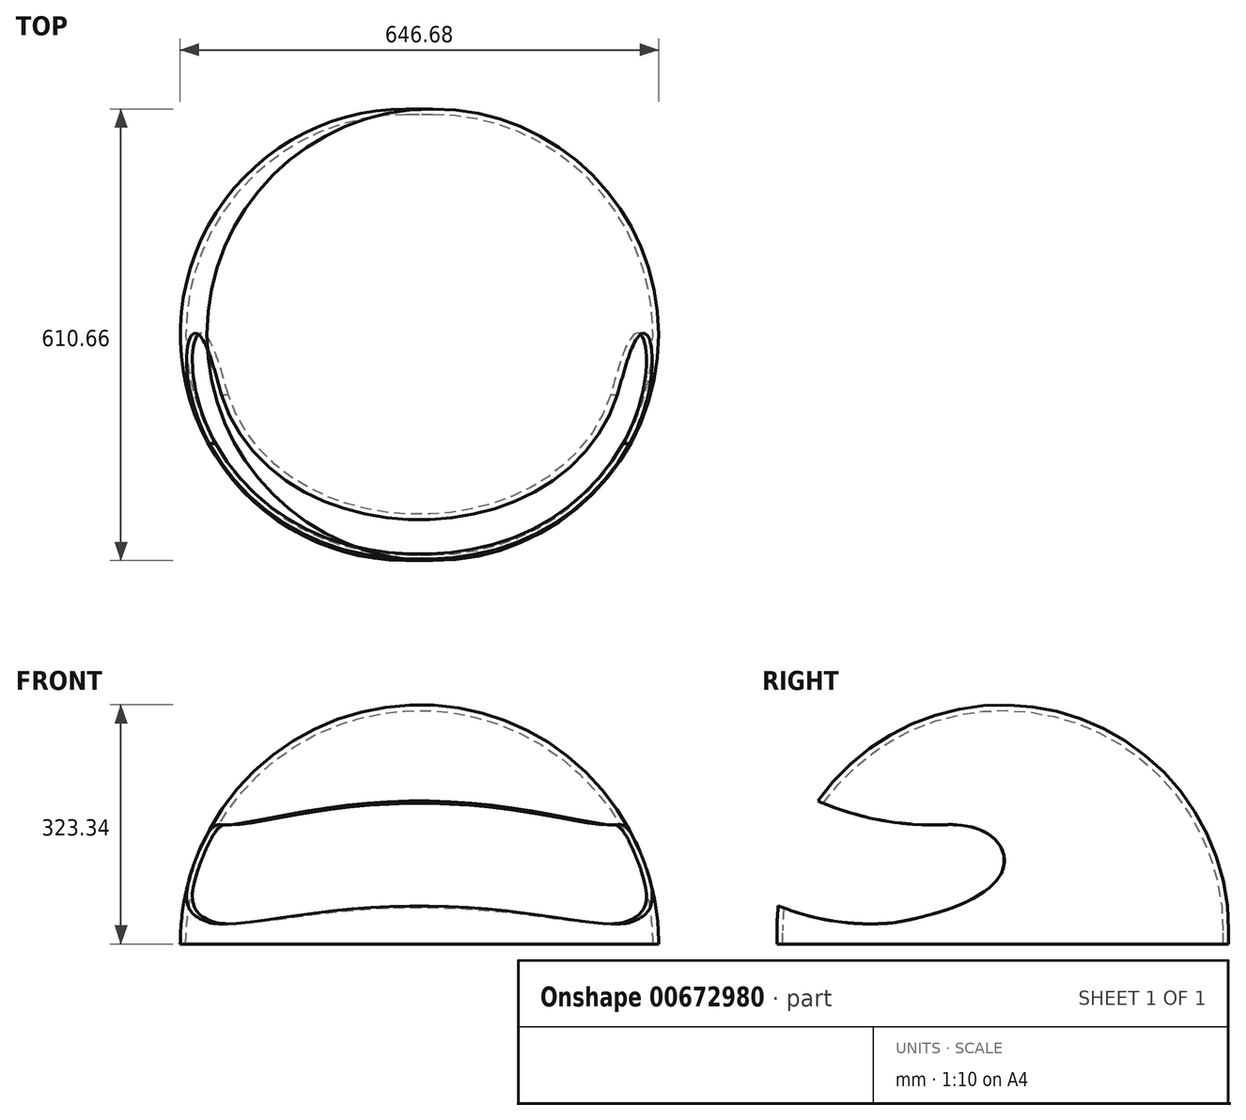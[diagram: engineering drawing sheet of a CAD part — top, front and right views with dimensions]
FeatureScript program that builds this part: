
annotation { "Feature Type Name" : "Feature", "Feature Type Description" : "" }
export const myFeature = defineFeature(function(context is Context, id is Id, definition is map)
    precondition{}
    {
        {
            var Q0;
            Q0=qCreatedBy(makeId("Top.planeOp"),FACE);
            var sketch = newSketch(context, id + "F0", { "sketchPlane" : qUnion([Q0])});
            skArc(sketch, "E0", {"start": v(0, -289.9) * mm, "mid": v(323.34, 14.9) * mm, "end": v(0, 319.7) * mm});
            skLineSegment(sketch, "E1", {"start": v(0, 341.68) * mm, "end": v(0, -321.3) * mm, "construction": true});
            skLineSegment(sketch, "E2", {"start": v(0, 319.7) * mm, "end": v(0, -289.9) * mm});
            skSolve(sketch);
        }
        {
            var Q0;
            Q0 = qSketchRegion(id + "F0", true);
            var Q1;
            Q1=sQuery(id+"F0.wireOp",EDGE,"E0");
            var Q2;
            Q2=sQuery(id+"F0.wireOp",EDGE,"E1");
            revolve(context, id + "F1", {"entities" : qUnion([Q0]), "surfaceEntities" : qUnion([Q1]), "axis" : qUnion([Q2]), "revolveType" : RevolveType.TWO_DIRECTIONS, "angle" : 180 * degree, "angleBack" : 360 * degree});
        }
        {
            var Q0;
            Q0=makeQuery(id+"F1.opRevolve","CAP_FACE",FACE,{"disambiguationData":[OSD([sQuery(id+"F0.wireOp",EDGE,"E0"),sQuery(id+"F0.wireOp",EDGE,"E2")])],"isStart":false});
            shell(context, id + "F2", {"entities" : qUnion([Q0]), "thickness" : 7.62 * mm});
        }
        {
            var Q0;
            Q0=qCreatedBy(makeId("Right.planeOp"),FACE);
            cPlane(context, id + "F3", {"entities" : qUnion([Q0]), "cplaneType" : CPlaneType.OFFSET, "offset" : 497.84 * mm, "width" : 152.4 * mm, "height" : 152.4 * mm});
        }
        {
            var Q0;
            Q0=qCreatedBy(id+"F3.planeOp",FACE);
            var sketch = newSketch(context, id + "F4", { "sketchPlane" : qUnion([Q0])});
            skArc(sketch, "E3", {"start": v(-315.15, 239.57) * mm, "mid": v(-197.38, 179.23) * mm, "end": v(-66.3, 161.05) * mm});
            skArc(sketch, "E4", {"start": v(-400.55, 126.3) * mm, "mid": v(-277.43, 47.22) * mm, "end": v(-132.27, 28.7) * mm});
            skLineSegment(sketch, "E5", {"start": v(-315.15, 239.57) * mm, "end": v(-400.55, 126.3) * mm});
            skFitSpline(sketch, "E6", {"points": [v(-66.3, 161.05) * mm, v(16.59, 107.22) * mm, v(-132.27, 28.7) * mm], "startDerivative": vector(419.18, 27.97) * mm, "endDerivative": vector(-459.8, -81.89) * mm});
            skSolve(sketch);
        }
        {
            var Q0;
            Q0 = qSketchRegion(id + "F4", true);
            var Q1;
            Q1 = qConstructionFilter(qBodyType(qCreatedBy(id + "F4" ,EDGE), BodyType.WIRE), ConstructionObject.NO);
            extrude(context, id + "F5", {"entities" : qUnion([Q0]), "operationType" : NewBodyOperationType.REMOVE, "surfaceEntities" : qUnion([Q1]), "endBound" : BoundingType.THROUGH_ALL, "oppositeDirection" : true, "depth" : 25.4 * mm, "offsetDistance" : 25.4 * mm});
        }
    });
